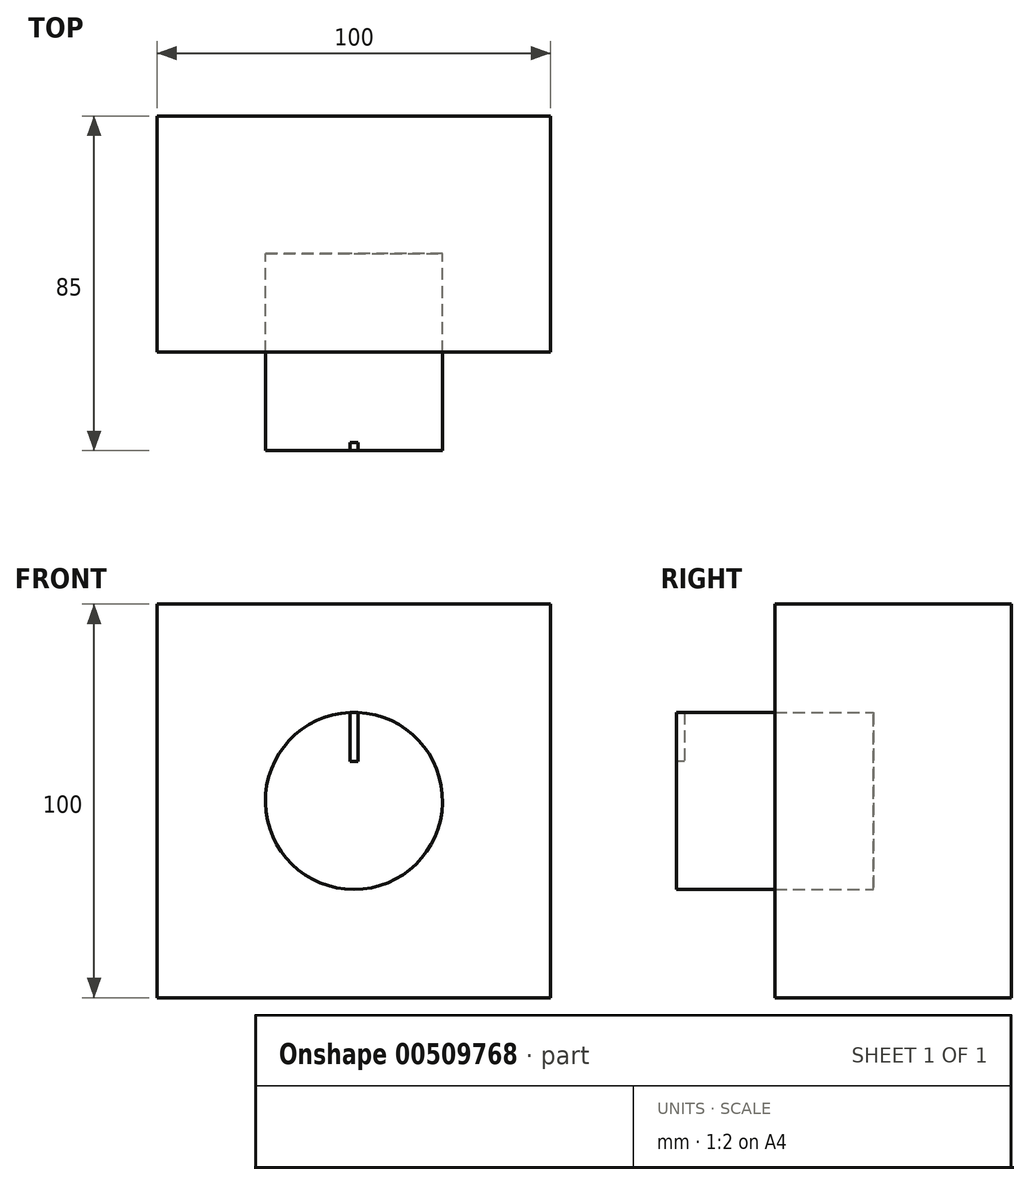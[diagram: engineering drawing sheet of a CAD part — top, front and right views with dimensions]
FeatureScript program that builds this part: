
annotation { "Feature Type Name" : "Feature", "Feature Type Description" : "" }
export const myFeature = defineFeature(function(context is Context, id is Id, definition is map)
    precondition{}
    {
        {
            var Q0;
            Q0=qCreatedBy(makeId("Front.planeOp"),FACE);
            var sketch = newSketch(context, id + "F0", { "sketchPlane" : qUnion([Q0])});
            skLineSegment(sketch, "E0.bottom", {"start": v(0, 0) * mm, "end": v(100, 0) * mm});
            skLineSegment(sketch, "E0.top", {"start": v(0, -100) * mm, "end": v(100, -100) * mm});
            skLineSegment(sketch, "E0.left", {"start": v(0, 0) * mm, "end": v(0, -100) * mm});
            skLineSegment(sketch, "E0.right", {"start": v(100, 0) * mm, "end": v(100, -100) * mm});
            skSolve(sketch);
        }
        {
            var Q0;
            Q0 = qSketchRegion(id + "F0", true);
            extrude(context, id + "F1", {"entities" : qUnion([Q0]), "depth" : 60 * mm});
        }
        {
            var Q0;
            Q0=makeQuery(id+"F1.opExtrude","CAP_FACE",FACE,{"disambiguationData":[OSD([sQuery(id+"F0.wireOp",EDGE,"E0.bottom"),sQuery(id+"F0.wireOp",EDGE,"E0.top"),sQuery(id+"F0.wireOp",EDGE,"E0.left"),sQuery(id+"F0.wireOp",EDGE,"E0.right")])],"isStart":false});
            var sketch = newSketch(context, id + "F2", { "sketchPlane" : qUnion([Q0])});
            skCircle(sketch, "E1", {"center": v(50, -50) * mm, "radius": 22.5 * mm});
            skSolve(sketch);
        }
        {
            var Q0;
            Q0 = qSketchRegion(id + "F2", true);
            extrude(context, id + "F3", {"entities" : qUnion([Q0]), "depth" : 25 * mm, "hasSecondDirection" : true, "secondDirectionOppositeDirection" : true, "secondDirectionDepth" : 25 * mm});
        }
        {
            var Q0;
            Q0=makeQuery(id+"F3.opExtrude","CAP_FACE",FACE,{"disambiguationData":[OSD([sQuery(id+"F2.wireOp",EDGE,"E1")])],"isStart":false});
            var sketch = newSketch(context, id + "F4", { "sketchPlane" : qUnion([Q0])});
            skLineSegment(sketch, "E2.bottom", {"start": v(49, -15) * mm, "end": v(51, -15) * mm});
            skLineSegment(sketch, "E2.top", {"start": v(49, -40) * mm, "end": v(51, -40) * mm});
            skLineSegment(sketch, "E2.left", {"start": v(49, -15) * mm, "end": v(49, -40) * mm});
            skLineSegment(sketch, "E2.right", {"start": v(51, -15) * mm, "end": v(51, -40) * mm});
            skSolve(sketch);
        }
        {
            var Q0;
            Q0 = qSketchRegion(id + "F4", true);
            extrude(context, id + "F5", {"entities" : qUnion([Q0]), "operationType" : NewBodyOperationType.REMOVE, "oppositeDirection" : true, "depth" : 2 * mm});
        }
    });
